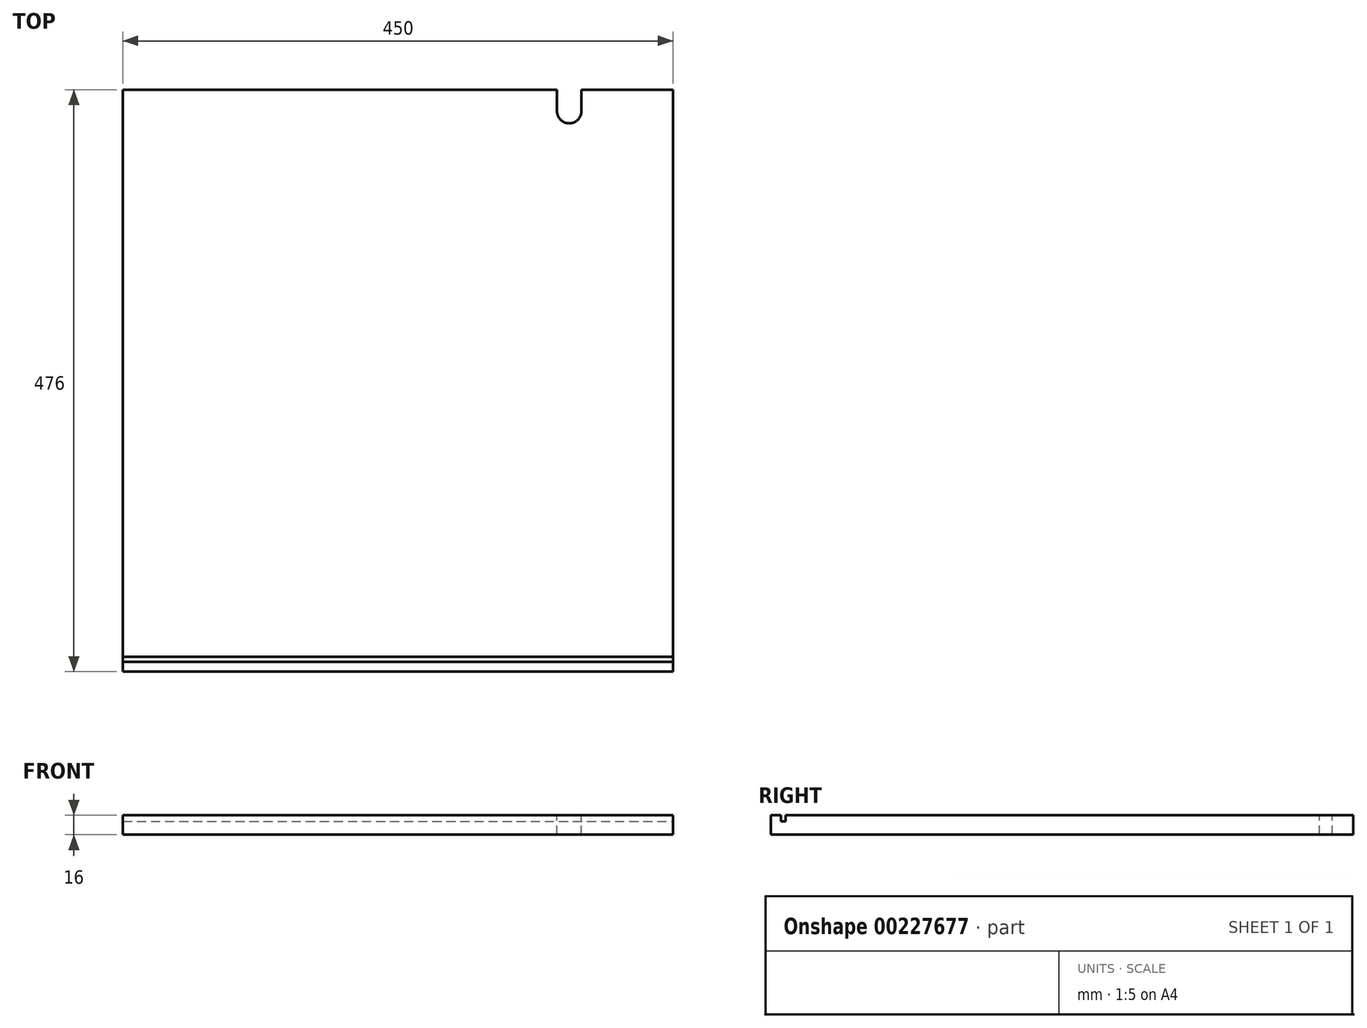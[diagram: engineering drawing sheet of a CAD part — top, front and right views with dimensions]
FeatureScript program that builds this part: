
annotation { "Feature Type Name" : "Feature", "Feature Type Description" : "" }
export const myFeature = defineFeature(function(context is Context, id is Id, definition is map)
    precondition{}
    {
        {
            var Q0;
            Q0=qCreatedBy(makeId("Top.planeOp"),FACE);
            var sketch = newSketch(context, id + "F0", { "sketchPlane" : qUnion([Q0])});
            skLineSegment(sketch, "E0.bottom", {"start": v(225, -238) * mm, "end": v(-225, -238) * mm});
            skLineSegment(sketch, "E0.top", {"start": v(225, 238) * mm, "end": v(-225, 238) * mm});
            skLineSegment(sketch, "E0.left", {"start": v(225, -238) * mm, "end": v(225, 238) * mm});
            skLineSegment(sketch, "E0.right", {"start": v(-225, -238) * mm, "end": v(-225, 238) * mm});
            skPoint(sketch, "E0.middle", {"position": v(0, 0) * mm});
            skSolve(sketch);
        }
        {
            var Q0;
            Q0 = qSketchRegion(id + "F0", true);
            extrude(context, id + "F1", {"entities" : qUnion([Q0]), "depth" : 16 * mm, "symmetric" : true});
        }
        {
            var Q0;
            Q0=makeQuery(id+"F1.opExtrude","CAP_FACE",FACE,{"disambiguationData":[OSD([sQuery(id+"F0.wireOp",EDGE,"E0.bottom"),sQuery(id+"F0.wireOp",EDGE,"E0.top"),sQuery(id+"F0.wireOp",EDGE,"E0.left"),sQuery(id+"F0.wireOp",EDGE,"E0.right")])],"isStart":false});
            var sketch = newSketch(context, id + "F2", { "sketchPlane" : qUnion([Q0])});
            skCircle(sketch, "E1", {"center": v(140, 220.5) * mm, "radius": 10 * mm});
            skLineSegment(sketch, "E2", {"start": v(130, 220.94) * mm, "end": v(130, 238) * mm});
            skLineSegment(sketch, "E3", {"start": v(150, 220.06) * mm, "end": v(150, 238) * mm});
            skSolve(sketch);
        }
        {
            var Q0;
            Q0 = qSketchRegion(id + "F2", true);
            var Q1;
            {var subQ0=sQuery(id+"F2.wireOp",EDGE,"fFE1UMWJ-B5r0-XRSC-vrcq-CDvjEmDyPfjg");Q1=makeQuery(id+"F2.imprint","IMPRINT",FACE,{"disambiguationData":[TD([[makeQuery(id+"F2.imprint","IMPRINT",EDGE,{"derivedFrom":subQ0}),1.0]])]});}
            var Q2;
            {var subQ0=sQuery(id+"F2.wireOp",EDGE,"E2");Q2=makeQuery(id+"F2.imprint","IMPRINT",FACE,{"disambiguationData":[TD([[makeQuery(id+"F2.imprint","IMPRINT",EDGE,{"derivedFrom":subQ0}),-1.0]])]});}
            extrude(context, id + "F3", {"entities" : qUnion([Q0, Q1, Q2]), "operationType" : NewBodyOperationType.REMOVE, "endBound" : BoundingType.THROUGH_ALL, "oppositeDirection" : true, "depth" : 25 * mm});
        }
        {
            var Q0;
            Q0=makeQuery(id+"F1.opExtrude","SWEPT_FACE",FACE,{"disambiguationData":[OSD([sQuery(id+"F0.wireOp",EDGE,"E0.left")])]});
            var sketch = newSketch(context, id + "F4", { "sketchPlane" : qUnion([Q0])});
            skLineSegment(sketch, "E4.bottom", {"start": v(-230, 8) * mm, "end": v(-226, 8) * mm});
            skLineSegment(sketch, "E4.top", {"start": v(-230, 3) * mm, "end": v(-226, 3) * mm});
            skLineSegment(sketch, "E4.left", {"start": v(-230, 8) * mm, "end": v(-230, 3) * mm});
            skLineSegment(sketch, "E4.right", {"start": v(-226, 8) * mm, "end": v(-226, 3) * mm});
            skSolve(sketch);
        }
        {
            var Q0;
            Q0 = qSketchRegion(id + "F4", true);
            extrude(context, id + "F5", {"entities" : qUnion([Q0]), "operationType" : NewBodyOperationType.REMOVE, "endBound" : BoundingType.THROUGH_ALL, "oppositeDirection" : true, "depth" : 25 * mm});
        }
    });
